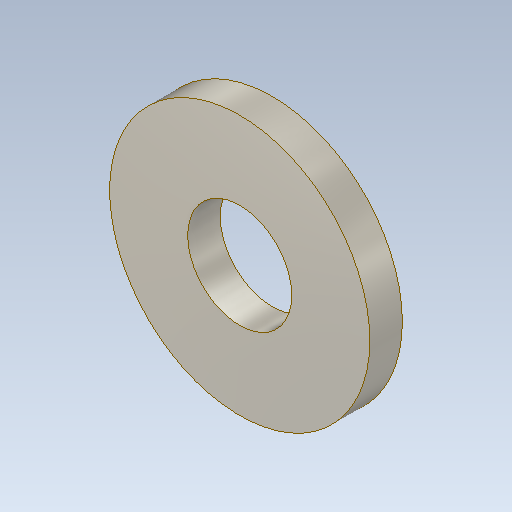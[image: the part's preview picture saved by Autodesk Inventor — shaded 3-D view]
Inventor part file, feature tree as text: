
AUTODESK INVENTOR PART (.ipt)
format: ipt  version: 2020.2 (Build 242310000, 310)  size: 98,304 bytes
history: native  units: mm
features: other x1, extrude x1, sketch x1
ambient origin geometry x8: Origin, YZ Plane, XZ Plane, XY Plane, X Axis, Y Axis, Z Axis, Center Point
bodies: Body1 (feature_tree)
feature tree (3):
  other  "ソリッド1"
  extrude  "押し出し1"  Depth=8.0mm
  sketch  "スケッチ1"
